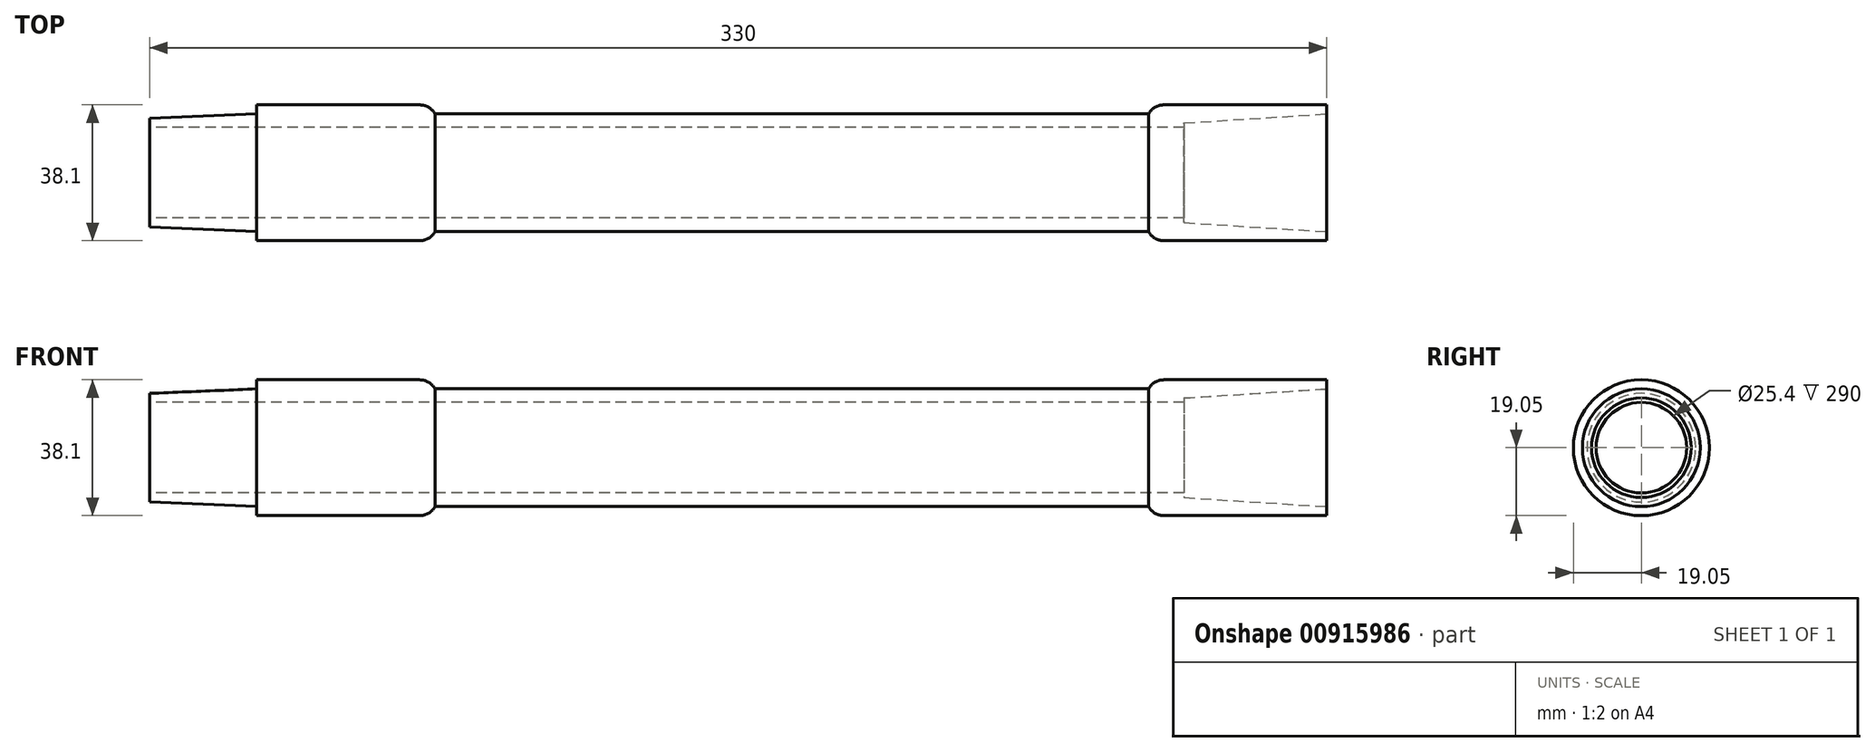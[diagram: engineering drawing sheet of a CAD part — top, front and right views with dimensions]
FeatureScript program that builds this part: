
annotation { "Feature Type Name" : "Feature", "Feature Type Description" : "" }
export const myFeature = defineFeature(function(context is Context, id is Id, definition is map)
    precondition{}
    {
        {
            var Q0;
            Q0=qCreatedBy(makeId("Front.planeOp"),FACE);
            var sketch = newSketch(context, id + "F0", { "sketchPlane" : qUnion([Q0])});
            skLineSegment(sketch, "E0", {"start": v(0, 12.7) * mm, "end": v(0, 15.24) * mm});
            skLineSegment(sketch, "E1", {"start": v(80, 16.51) * mm, "end": v(80, 19.05) * mm});
            skLineSegment(sketch, "E2", {"start": v(280, 16.51) * mm, "end": v(280, 19.05) * mm});
            skLineSegment(sketch, "E3", {"start": v(290, 12.7) * mm, "end": v(290, 13.97) * mm});
            skLineSegment(sketch, "E4", {"start": v(280, 19.05) * mm, "end": v(330, 19.05) * mm});
            skLineSegment(sketch, "E5", {"start": v(30, 19.05) * mm, "end": v(80, 19.05) * mm});
            skLineSegment(sketch, "E6", {"start": v(280, 16.51) * mm, "end": v(80, 16.51) * mm});
            skLineSegment(sketch, "E7", {"start": v(330, 16.51) * mm, "end": v(330, 19.05) * mm});
            skLineSegment(sketch, "E8", {"start": v(290, 13.97) * mm, "end": v(330, 16.5) * mm});
            skPoint(sketch, "E9.end.orphan", {"position": v(330, 0) * mm});
            skLineSegment(sketch, "E10", {"start": v(30, 12.7) * mm, "end": v(0, 12.7) * mm});
            skLineSegment(sketch, "E11", {"start": v(30, 12.7) * mm, "end": v(290, 12.7) * mm});
            skLineSegment(sketch, "E12", {"start": v(0, 15.24) * mm, "end": v(30, 16.51) * mm});
            skLineSegment(sketch, "E13", {"start": v(30, 16.51) * mm, "end": v(30, 19.05) * mm});
            skPoint(sketch, "E14.end.orphan", {"position": v(290, 0) * mm});
            skPoint(sketch, "E15.end.orphan", {"position": v(80, 0) * mm});
            skSolve(sketch);
        }
        {
            var Q0;
            Q0=qCreatedBy(makeId("Right.planeOp"),FACE);
            var sketch = newSketch(context, id + "F1", { "sketchPlane" : qUnion([Q0])});
            skLineSegment(sketch, "E16", {"start": v(0, 0) * mm, "end": v(0, 12.7) * mm});
            skCircle(sketch, "E17", {"center": v(0, 0) * mm, "radius": 12.7 * mm});
            skSolve(sketch);
        }
        {
            var Q0;
            Q0 = qSketchRegion(id + "F0", true);
            var Q1;
            Q1=sQuery(id+"F1.wireOp",EDGE,"E17");
            revolve(context, id + "F2", {"surfaceOperationType" : NewSurfaceOperationType.NEW, "entities" : qUnion([Q0]), "axis" : qUnion([Q1]), "revolveType" : RevolveType.FULL});
        }
        {
            var Q0;
            Q0=makeQuery(id+"F2.opRevolve","SWEPT_EDGE",EDGE,{"disambiguationData":[OSD([sQuery(id+"F0.wireOp",EDGE,"E1"),sQuery(id+"F0.wireOp",EDGE,"E5")])]});
            var Q1;
            Q1=makeQuery(id+"F2.opRevolve","SWEPT_EDGE",EDGE,{"disambiguationData":[OSD([sQuery(id+"F0.wireOp",EDGE,"E2"),sQuery(id+"F0.wireOp",EDGE,"E4")])]});
            fillet(context, id + "F3", {"entities" : qUnion([Q0, Q1]), "radius" : 5 * mm, "tangentPropagation" : true, "allowEdgeOverflow" : false});
        }
    });
